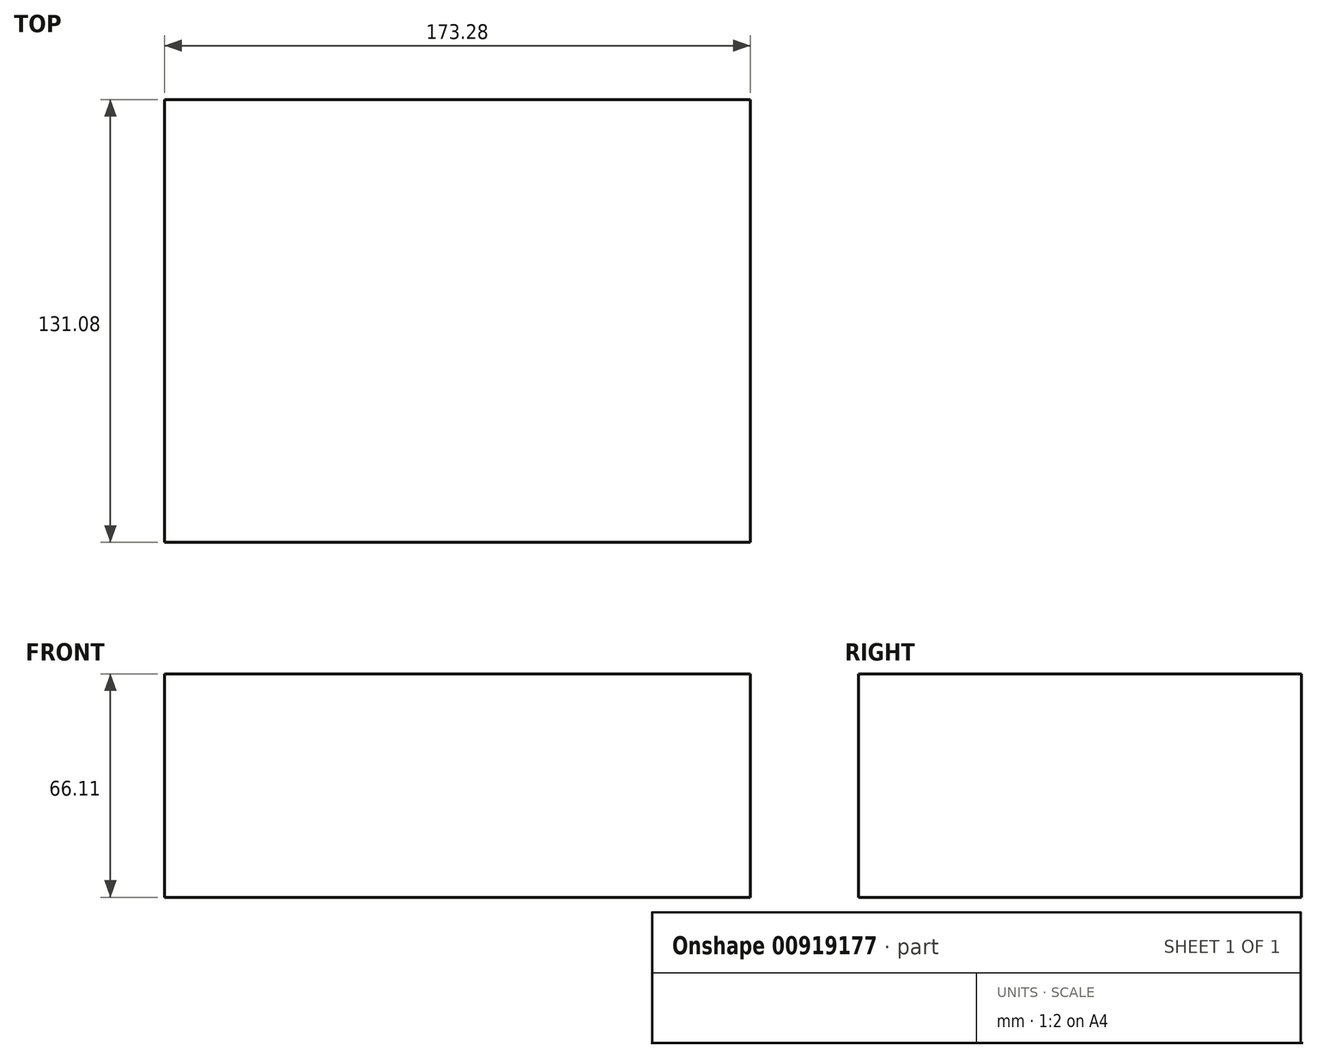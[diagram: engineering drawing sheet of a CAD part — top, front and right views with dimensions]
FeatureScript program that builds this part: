
annotation { "Feature Type Name" : "Feature", "Feature Type Description" : "" }
export const myFeature = defineFeature(function(context is Context, id is Id, definition is map)
    precondition{}
    {
        {
            var Q0;
            Q0=qCreatedBy(makeId("Top.planeOp"),FACE);
            var sketch = newSketch(context, id + "F0", { "sketchPlane" : qUnion([Q0])});
            skLineSegment(sketch, "E0.bottom", {"start": v(86.64, -65.54) * mm, "end": v(-86.64, -65.54) * mm});
            skLineSegment(sketch, "E0.top", {"start": v(86.64, 65.54) * mm, "end": v(-86.64, 65.54) * mm});
            skLineSegment(sketch, "E0.left", {"start": v(86.64, -65.54) * mm, "end": v(86.64, 65.54) * mm});
            skLineSegment(sketch, "E0.right", {"start": v(-86.64, -65.54) * mm, "end": v(-86.64, 65.54) * mm});
            skPoint(sketch, "E0.middle", {"position": v(0, 0) * mm});
            skSolve(sketch);
        }
        {
            var Q0;
            Q0 = qSketchRegion(id + "F0", true);
            extrude(context, id + "F1", {"entities" : qUnion([Q0]), "depth" : 66.11 * mm, "offsetDistance" : 25.4 * mm});
        }
    });
